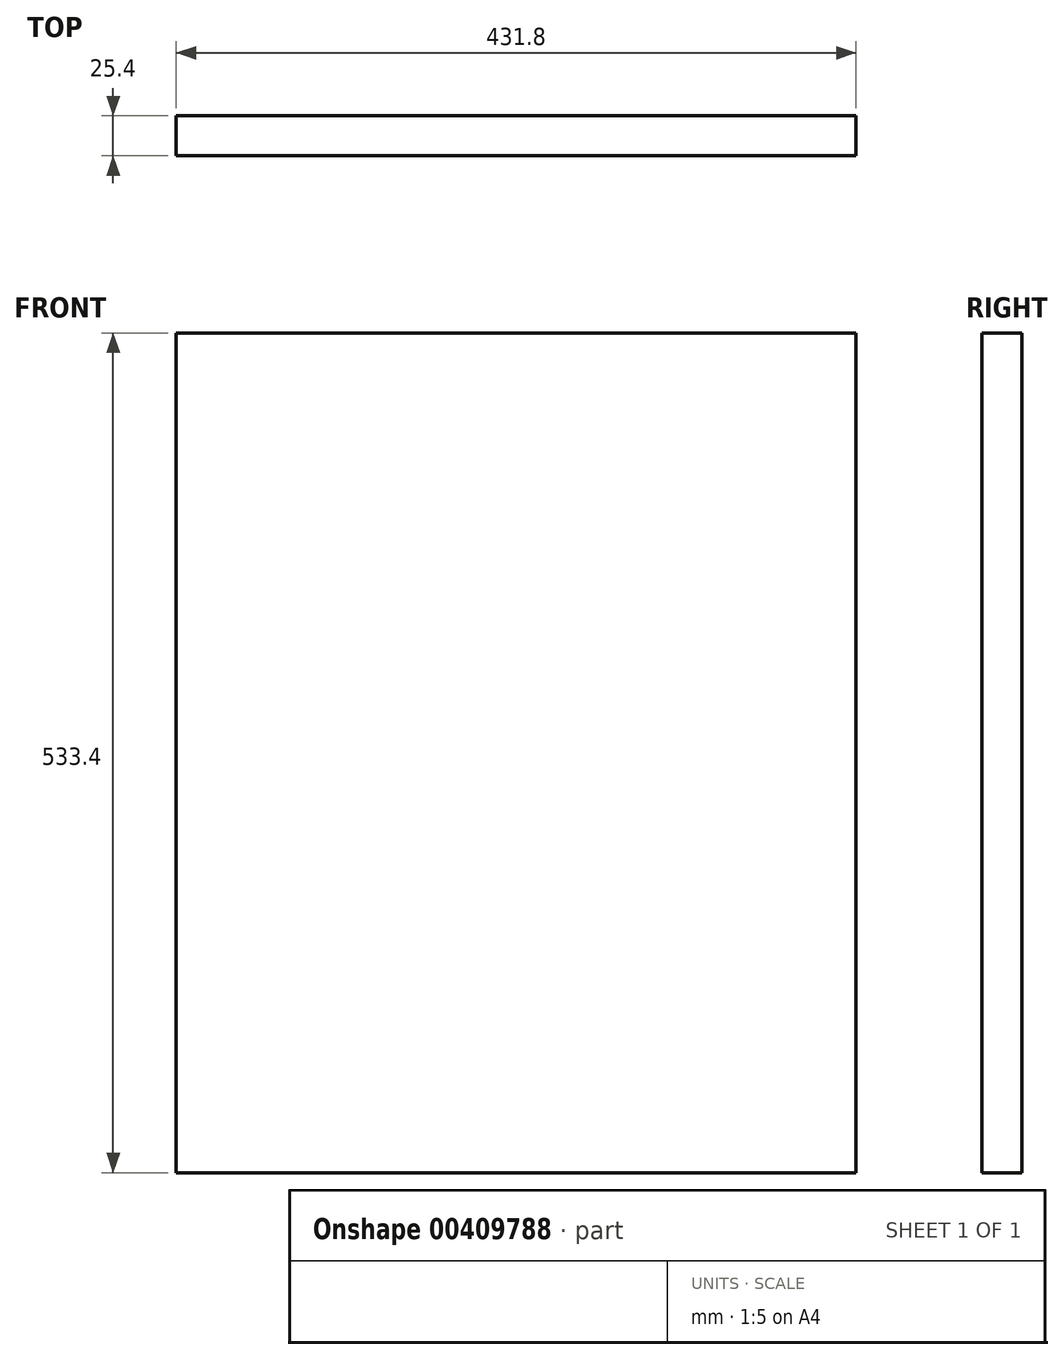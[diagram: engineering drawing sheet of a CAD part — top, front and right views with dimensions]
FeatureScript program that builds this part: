
annotation { "Feature Type Name" : "Feature", "Feature Type Description" : "" }
export const myFeature = defineFeature(function(context is Context, id is Id, definition is map)
    precondition{}
    {
        {
            var Q0;
            Q0=qCreatedBy(makeId("Front.planeOp"),FACE);
            var sketch = newSketch(context, id + "F0", { "sketchPlane" : qUnion([Q0])});
            skLineSegment(sketch, "E0.bottom", {"start": v(215.9, -266.7) * mm, "end": v(-215.9, -266.7) * mm});
            skLineSegment(sketch, "E0.top", {"start": v(215.9, 266.7) * mm, "end": v(-215.9, 266.7) * mm});
            skLineSegment(sketch, "E0.left", {"start": v(215.9, -266.7) * mm, "end": v(215.9, 266.7) * mm});
            skLineSegment(sketch, "E0.right", {"start": v(-215.9, -266.7) * mm, "end": v(-215.9, 266.7) * mm});
            skPoint(sketch, "E0.middle", {"position": v(0, 0) * mm});
            skSolve(sketch);
        }
        {
            var Q0;
            Q0=makeQuery(id+"F0.imprint","IMPRINT",FACE,{"disambiguationData":[TD([[makeQuery(id+"F0.imprint","IMPRINT",EDGE,{"derivedFrom":sQuery(id+"F0.wireOp",EDGE,"E0.bottom")}),-1.0]])]});
            extrude(context, id + "F1", {"entities" : qUnion([Q0]), "depth" : 25.4 * mm});
        }
    });
